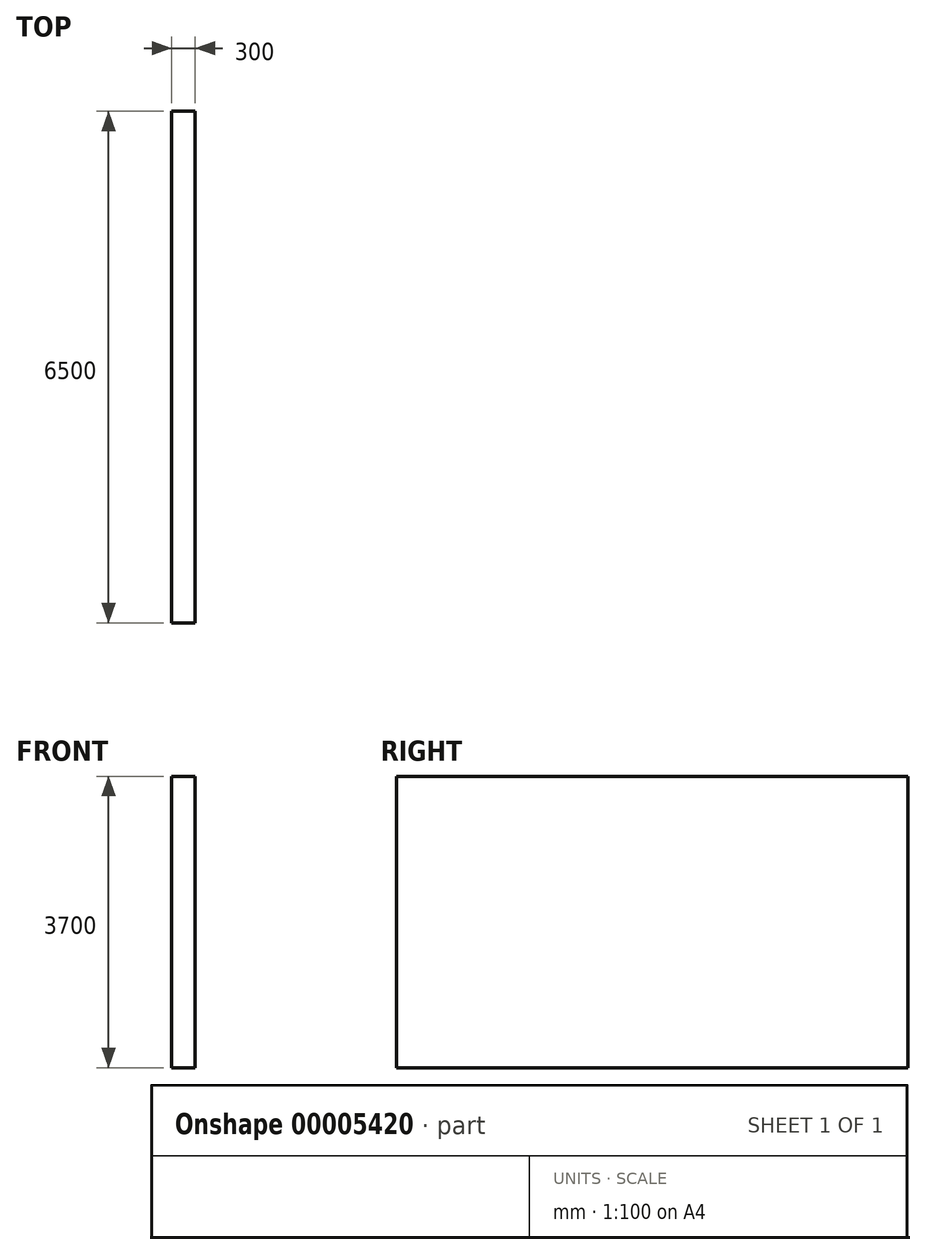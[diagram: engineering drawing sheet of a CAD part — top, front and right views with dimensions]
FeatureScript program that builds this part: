
annotation { "Feature Type Name" : "Feature", "Feature Type Description" : "" }
export const myFeature = defineFeature(function(context is Context, id is Id, definition is map)
    precondition{}
    {
        {
            var Q0;
            Q0=qCreatedBy(makeId("Right.planeOp"),FACE);
            var sketch = newSketch(context, id + "F0", { "sketchPlane" : qUnion([Q0])});
            skLineSegment(sketch, "E0.bottom", {"start": v(-3257.26, 1971.58) * mm, "end": v(3242.74, 1971.58) * mm});
            skLineSegment(sketch, "E0.top", {"start": v(-3257.26, -1728.42) * mm, "end": v(3242.74, -1728.42) * mm});
            skLineSegment(sketch, "E0.left", {"start": v(-3257.26, 1971.58) * mm, "end": v(-3257.26, -1728.42) * mm});
            skLineSegment(sketch, "E0.right", {"start": v(3242.74, 1971.58) * mm, "end": v(3242.74, -1728.42) * mm});
            skSolve(sketch);
        }
        {
            var Q0;
            Q0=makeQuery(id+"F0.imprint","IMPRINT",FACE,{"disambiguationData":[TD([[makeQuery(id+"F0.imprint","IMPRINT",EDGE,{"derivedFrom":sQuery(id+"F0.wireOp",EDGE,"E0.bottom")}),-1.0]])]});
            extrude(context, id + "F1", {"entities" : qUnion([Q0]), "depth" : 300 * mm});
        }
    });
